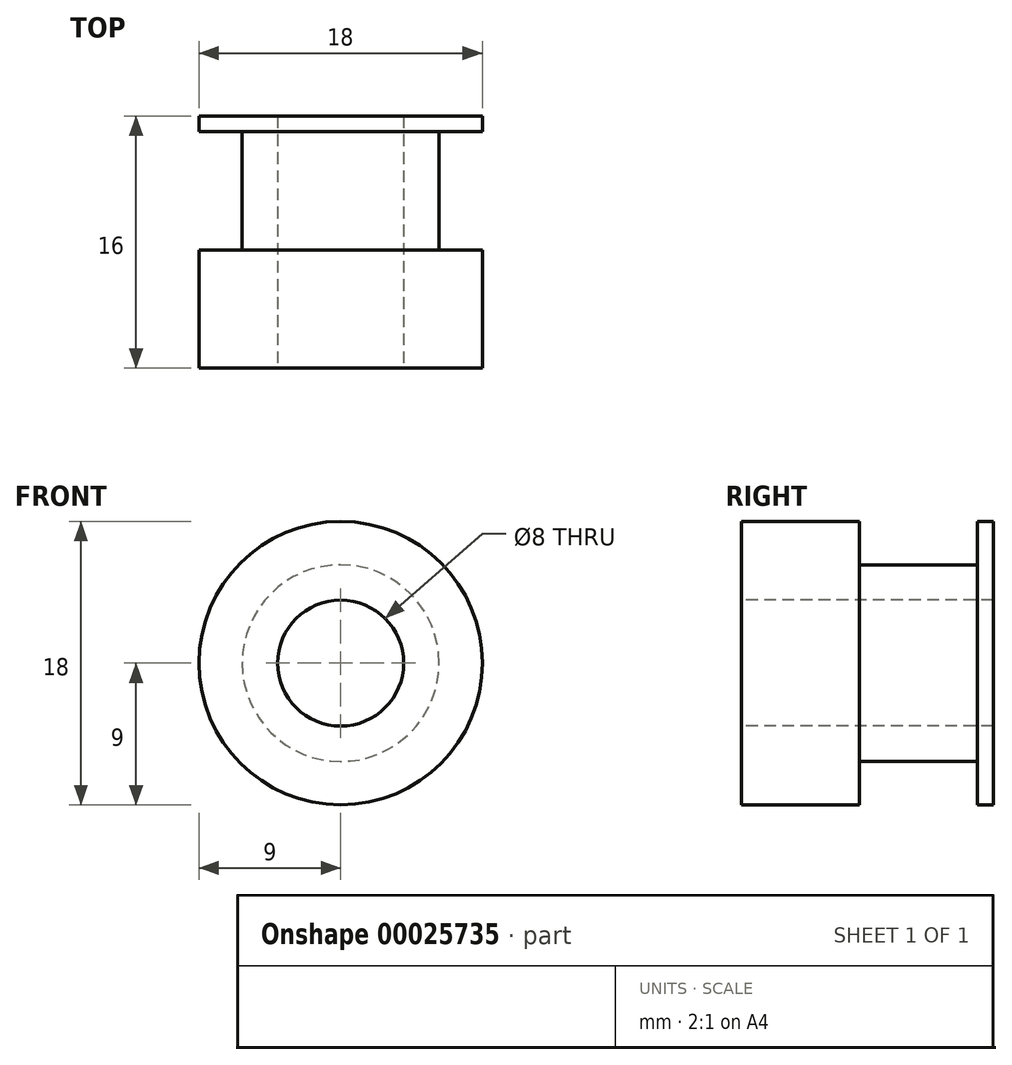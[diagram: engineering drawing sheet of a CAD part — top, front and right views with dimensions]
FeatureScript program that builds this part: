
annotation { "Feature Type Name" : "Feature", "Feature Type Description" : "" }
export const myFeature = defineFeature(function(context is Context, id is Id, definition is map)
    precondition{}
    {
        {
            var Q0;
            Q0=qCreatedBy(makeId("Right.planeOp"),FACE);
            var sketch = newSketch(context, id + "F0", { "sketchPlane" : qUnion([Q0])});
            skLineSegment(sketch, "E0", {"start": v(0, 0) * mm, "end": v(16, 0) * mm, "construction": true});
            skLineSegment(sketch, "E1", {"start": v(16, 0) * mm, "end": v(16, 4) * mm, "construction": true});
            skLineSegment(sketch, "E2", {"start": v(16, 4) * mm, "end": v(0, 4) * mm});
            skLineSegment(sketch, "E3", {"start": v(0, 4) * mm, "end": v(0, 9) * mm});
            skLineSegment(sketch, "E4", {"start": v(0, 9) * mm, "end": v(7.5, 9) * mm});
            skLineSegment(sketch, "E5", {"start": v(7.5, 9) * mm, "end": v(7.5, 6.25) * mm});
            skLineSegment(sketch, "E6", {"start": v(7.5, 6.25) * mm, "end": v(15, 6.25) * mm});
            skLineSegment(sketch, "E7", {"start": v(15, 6.25) * mm, "end": v(15, 9) * mm});
            skLineSegment(sketch, "E8", {"start": v(15, 9) * mm, "end": v(16, 9) * mm});
            skLineSegment(sketch, "E9", {"start": v(16, 9) * mm, "end": v(16, 4) * mm});
            skSolve(sketch);
        }
        {
            var Q0;
            Q0 = qSketchRegion(id + "F0", true);
            var Q1;
            Q1=sQuery(id+"F0.wireOp",EDGE,"E0");
            revolve(context, id + "F1", {"entities" : qUnion([Q0]), "axis" : qUnion([Q1]), "revolveType" : RevolveType.FULL});
        }
    });
